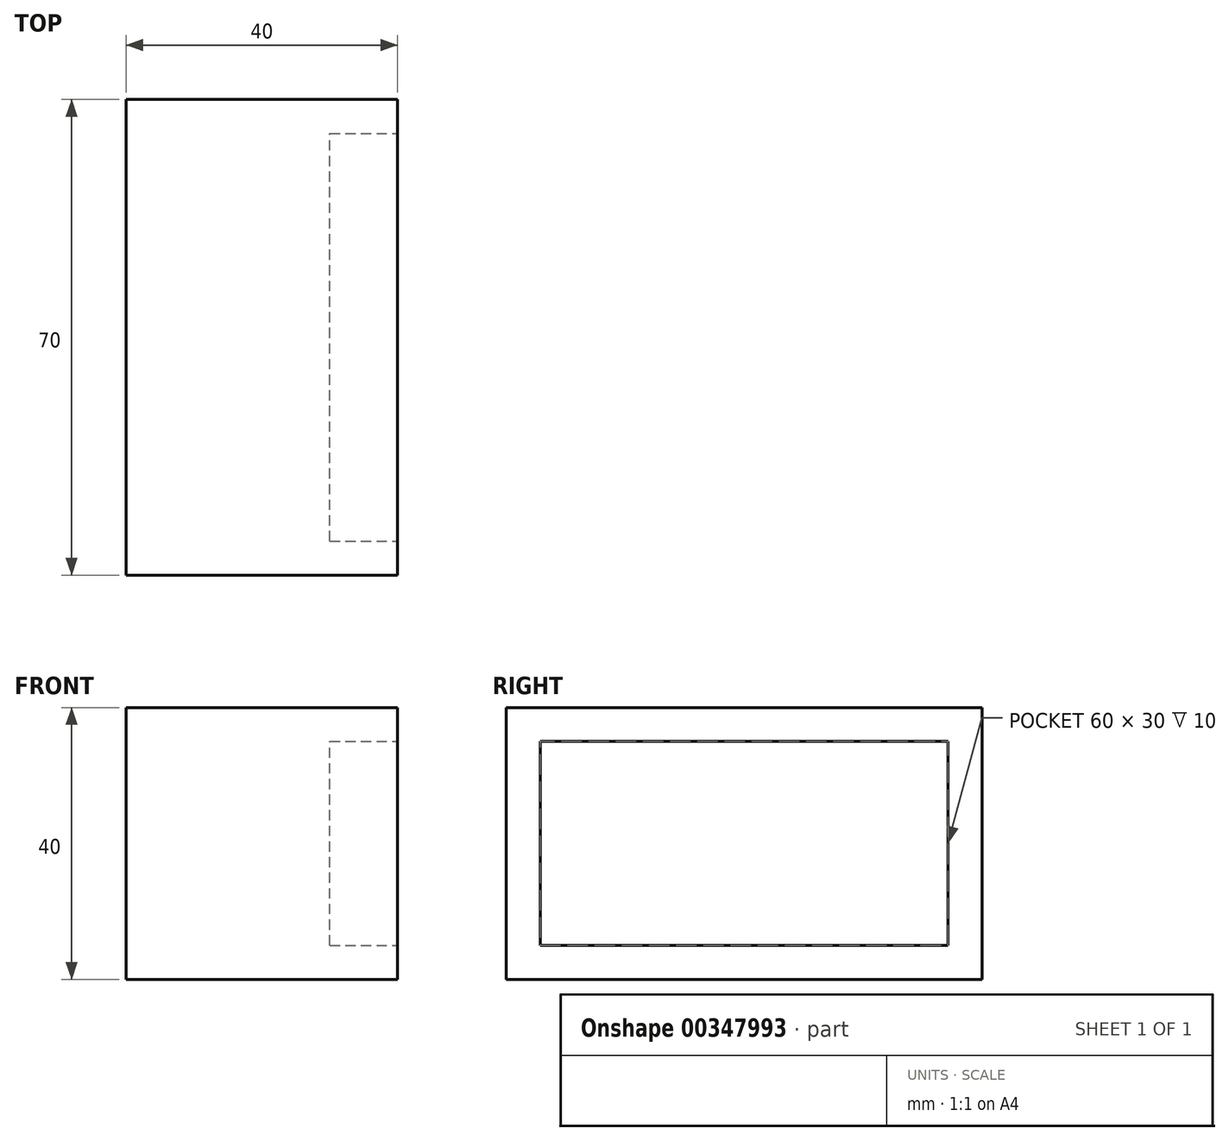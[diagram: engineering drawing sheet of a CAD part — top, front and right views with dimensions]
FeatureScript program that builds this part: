
annotation { "Feature Type Name" : "Feature", "Feature Type Description" : "" }
export const myFeature = defineFeature(function(context is Context, id is Id, definition is map)
    precondition{}
    {
        {
            var Q0;
            Q0=qCreatedBy(makeId("Right.planeOp"),FACE);
            var sketch = newSketch(context, id + "F0", { "sketchPlane" : qUnion([Q0])});
            skLineSegment(sketch, "E0", {"start": v(0, 0) * mm, "end": v(0, 40) * mm});
            skLineSegment(sketch, "E1", {"start": v(0, 40) * mm, "end": v(70, 40) * mm});
            skLineSegment(sketch, "E2", {"start": v(70, 40) * mm, "end": v(70, 0) * mm});
            skLineSegment(sketch, "E3", {"start": v(70, 0) * mm, "end": v(0, 0) * mm});
            skSolve(sketch);
        }
        {
            var Q0;
            Q0 = qSketchRegion(id + "F0", true);
            extrude(context, id + "F1", {"entities" : qUnion([Q0]), "depth" : 40 * mm});
        }
        {
            var Q0;
            Q0=makeQuery(id+"F1.opExtrude","CAP_FACE",FACE,{"disambiguationData":[OSD([sQuery(id+"F0.wireOp",EDGE,"E0"),sQuery(id+"F0.wireOp",EDGE,"E1"),sQuery(id+"F0.wireOp",EDGE,"E2"),sQuery(id+"F0.wireOp",EDGE,"E3")])],"isStart":false});
            var sketch = newSketch(context, id + "F2", { "sketchPlane" : qUnion([Q0])});
            skLineSegment(sketch, "E4.bottom", {"start": v(5, 5) * mm, "end": v(65, 5) * mm});
            skLineSegment(sketch, "E4.top", {"start": v(5, 35) * mm, "end": v(65, 35) * mm});
            skLineSegment(sketch, "E4.left", {"start": v(5, 5) * mm, "end": v(5, 35) * mm});
            skLineSegment(sketch, "E4.right", {"start": v(65, 5) * mm, "end": v(65, 35) * mm});
            skSolve(sketch);
        }
        {
            var Q0;
            Q0 = qSketchRegion(id + "F2", true);
            extrude(context, id + "F3", {"entities" : qUnion([Q0]), "operationType" : NewBodyOperationType.REMOVE, "oppositeDirection" : true, "depth" : 10 * mm});
        }
    });
